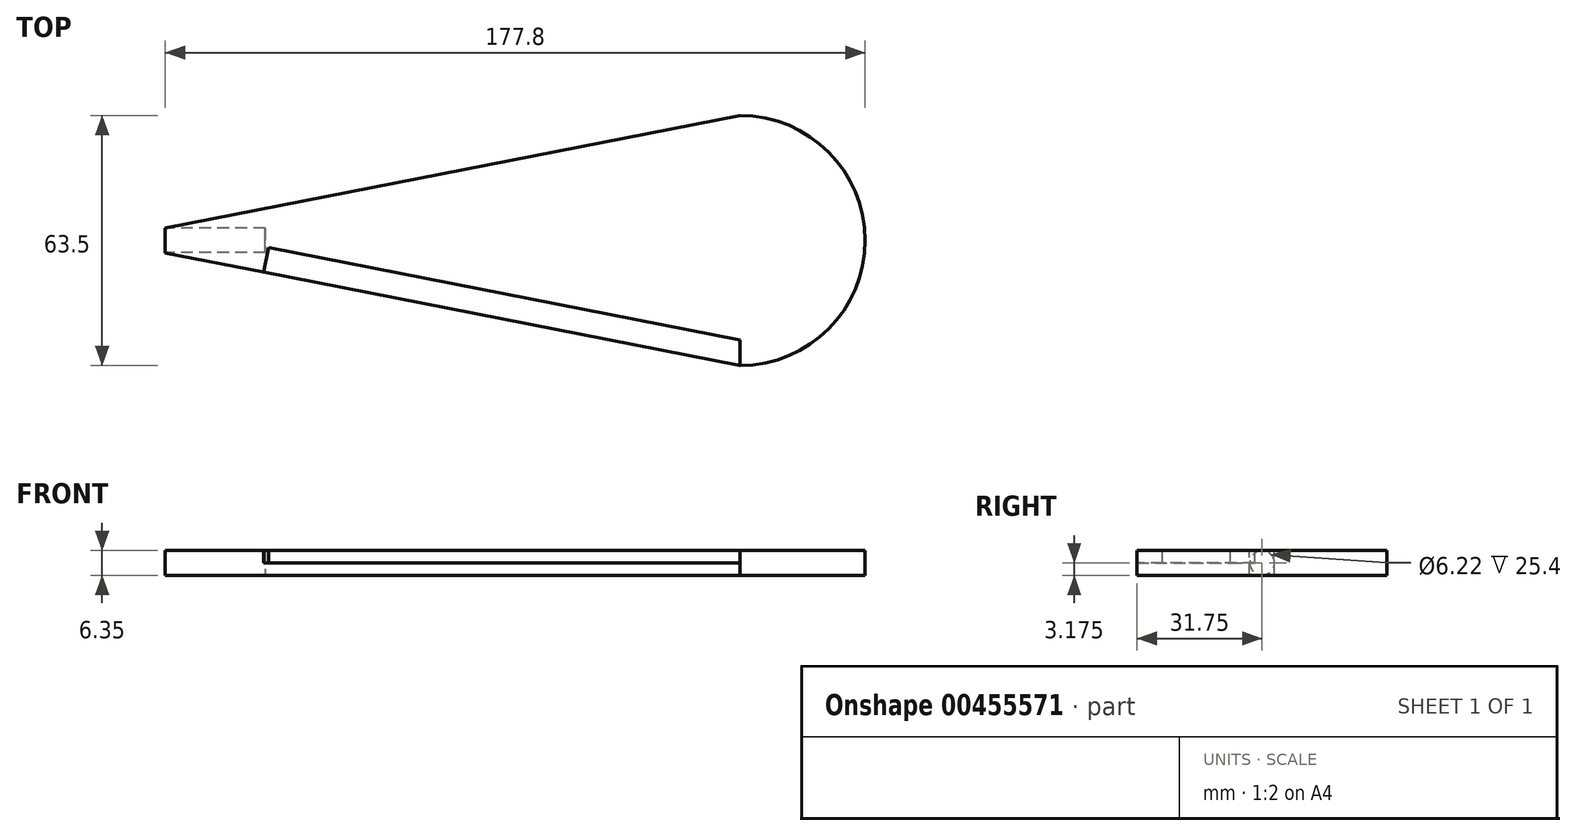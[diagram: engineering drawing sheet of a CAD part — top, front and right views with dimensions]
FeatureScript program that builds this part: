
annotation { "Feature Type Name" : "Feature", "Feature Type Description" : "" }
export const myFeature = defineFeature(function(context is Context, id is Id, definition is map)
    precondition{}
    {
        {
            var Q0;
            Q0=qCreatedBy(makeId("Top.planeOp"),FACE);
            var sketch = newSketch(context, id + "F0", { "sketchPlane" : qUnion([Q0])});
            skLineSegment(sketch, "E0", {"start": v(0, 0) * mm, "end": v(177.8, 0) * mm});
            skLineSegment(sketch, "E1", {"start": v(177.8, 0) * mm, "end": v(177.8, 63.5) * mm});
            skLineSegment(sketch, "E2", {"start": v(177.8, 63.5) * mm, "end": v(0, 63.5) * mm});
            skLineSegment(sketch, "E3", {"start": v(0, 63.5) * mm, "end": v(0, 0) * mm});
            skSolve(sketch);
        }
        {
            var Q0;
            Q0=makeQuery(id+"F0.imprint","IMPRINT",FACE,{"disambiguationData":[TD([[makeQuery(id+"F0.imprint","IMPRINT",EDGE,{"derivedFrom":sQuery(id+"F0.wireOp",EDGE,"E0")}),1.0]])]});
            extrude(context, id + "F1", {"entities" : qUnion([Q0]), "depth" : 6.35 * mm});
        }
        {
            var Q0;
            Q0=makeQuery(id+"F1.opExtrude","CAP_FACE",FACE,{"disambiguationData":[OSD([sQuery(id+"F0.wireOp",EDGE,"E0"),sQuery(id+"F0.wireOp",EDGE,"E1"),sQuery(id+"F0.wireOp",EDGE,"E2"),sQuery(id+"F0.wireOp",EDGE,"E3")])],"isStart":false});
            var sketch = newSketch(context, id + "F2", { "sketchPlane" : qUnion([Q0])});
            skArc(sketch, "E4", {"start": v(146.05, 0) * mm, "mid": v(177.8, 31.75) * mm, "end": v(146.05, 63.5) * mm});
            skSolve(sketch);
        }
        {
            var Q0;
            Q0 = qSketchRegion(id + "F2", true);
            var Q1;
            {var subQ0=sQuery(id+"F2.wireOp",EDGE,"E4");var subQ1=makeQuery(id+"F1.opExtrude","CAP_EDGE",EDGE,{"disambiguationData":[OSD([sQuery(id+"F0.wireOp",EDGE,"E2")])],"isStart":false});var subQ2=makeQuery(id+"F2.imprint","INTERSECT",VERTEX,{"derivedFrom":[subQ1,subQ0]});Q1=makeQuery(id+"F2.imprint","IMPRINT",FACE,{"disambiguationData":[TD([[makeQuery(id+"F2.imprint","IMPRINT",EDGE,{"disambiguationData":[TD([[subQ2,1.0]])],"derivedFrom":subQ0}),-1.0]])]});}
            var Q2;
            {var subQ0=sQuery(id+"F2.wireOp",EDGE,"E4");var subQ1=makeQuery(id+"F1.opExtrude","CAP_EDGE",EDGE,{"disambiguationData":[OSD([sQuery(id+"F0.wireOp",EDGE,"E0")])],"isStart":false});var subQ2=makeQuery(id+"F2.imprint","INTERSECT",VERTEX,{"derivedFrom":[subQ1,subQ0]});Q2=makeQuery(id+"F2.imprint","IMPRINT",FACE,{"disambiguationData":[TD([[makeQuery(id+"F2.imprint","IMPRINT",EDGE,{"disambiguationData":[TD([[subQ2,-1.0]])],"derivedFrom":subQ0}),-1.0]])]});}
            extrude(context, id + "F3", {"entities" : qUnion([Q0, Q1, Q2]), "operationType" : NewBodyOperationType.REMOVE, "oppositeDirection" : true, "depth" : 25.4 * mm});
        }
        {
            var Q0;
            Q0=makeQuery(id+"F1.opExtrude","CAP_FACE",FACE,{"disambiguationData":[OSD([sQuery(id+"F0.wireOp",EDGE,"E0"),sQuery(id+"F0.wireOp",EDGE,"E1"),sQuery(id+"F0.wireOp",EDGE,"E2"),sQuery(id+"F0.wireOp",EDGE,"E3")])],"isStart":false});
            var sketch = newSketch(context, id + "F4", { "sketchPlane" : qUnion([Q0])});
            skLineSegment(sketch, "E5", {"start": v(146.05, 63.5) * mm, "end": v(0, 34.93) * mm});
            skLineSegment(sketch, "E6", {"start": v(146.05, 0) * mm, "end": v(0, 28.58) * mm});
            skSolve(sketch);
        }
        {
            var Q0;
            {var subQ0=sQuery(id+"F4.wireOp",EDGE,"E5");Q0=makeQuery(id+"F4.imprint","IMPRINT",FACE,{"disambiguationData":[TD([[makeQuery(id+"F4.imprint","IMPRINT",EDGE,{"derivedFrom":subQ0}),-1.0]])]});}
            var Q1;
            {var subQ0=sQuery(id+"F4.wireOp",EDGE,"E6");Q1=makeQuery(id+"F4.imprint","IMPRINT",FACE,{"disambiguationData":[TD([[makeQuery(id+"F4.imprint","IMPRINT",EDGE,{"derivedFrom":subQ0}),1.0]])]});}
            extrude(context, id + "F5", {"entities" : qUnion([Q0, Q1]), "operationType" : NewBodyOperationType.REMOVE, "oppositeDirection" : true, "depth" : 25.4 * mm});
        }
        {
            var Q0;
            Q0=makeQuery(id+"F1.opExtrude","SWEPT_FACE",FACE,{"disambiguationData":[OSD([sQuery(id+"F0.wireOp",EDGE,"E3")])]});
            var sketch = newSketch(context, id + "F6", { "sketchPlane" : qUnion([Q0])});
            skCircle(sketch, "E7", {"center": v(-31.75, 3.17) * mm, "radius": 3.11 * mm});
            skPoint(sketch, "E7.centerSnap0", {"position": v(-31.75, 6.35) * mm});
            skPoint(sketch, "E7.centerSnap1", {"position": v(-28.58, 3.17) * mm});
            skSolve(sketch);
        }
        {
            var Q0;
            {var subQ0=sQuery(id+"F6.wireOp",EDGE,"E7");var subQ1=sQuery(id+"F0.wireOp",EDGE,"E3");var subQ2=makeQuery(id+"F6.imprint","INTERSECT",VERTEX,{"derivedFrom":[makeQuery(id+"F1.opExtrude","CAP_EDGE",EDGE,{"disambiguationData":[OSD([subQ1])],"isStart":false}),subQ0]});Q0=makeQuery(id+"F6.imprint","IMPRINT",FACE,{"disambiguationData":[TD([[makeQuery(id+"F6.imprint","IMPRINT",EDGE,{"disambiguationData":[TD([[subQ2,1.0]])],"derivedFrom":subQ0}),1.0]])]});}
            extrude(context, id + "F7", {"entities" : qUnion([Q0]), "operationType" : NewBodyOperationType.REMOVE, "oppositeDirection" : true, "depth" : 25.4 * mm});
        }
        {
            var Q0;
            Q0=makeQuery(id+"F1.opExtrude","CAP_FACE",FACE,{"disambiguationData":[OSD([sQuery(id+"F0.wireOp",EDGE,"E0"),sQuery(id+"F0.wireOp",EDGE,"E1"),sQuery(id+"F0.wireOp",EDGE,"E2"),sQuery(id+"F0.wireOp",EDGE,"E3")])],"isStart":false});
            var sketch = newSketch(context, id + "F8", { "sketchPlane" : qUnion([Q0])});
            skLineSegment(sketch, "E8", {"start": v(25.02, 23.68) * mm, "end": v(26.24, 29.91) * mm});
            skLineSegment(sketch, "E9", {"start": v(26.24, 29.91) * mm, "end": v(146.05, 6.47) * mm});
            skLineSegment(sketch, "E10", {"start": v(146.05, 6.47) * mm, "end": v(146.05, 0) * mm});
            skLineSegment(sketch, "E11", {"start": v(146.05, 0) * mm, "end": v(25.02, 23.68) * mm});
            skSolve(sketch);
        }
        {
            var Q0;
            Q0 = qSketchRegion(id + "F8", true);
            extrude(context, id + "F9", {"entities" : qUnion([Q0]), "operationType" : NewBodyOperationType.REMOVE, "oppositeDirection" : true, "depth" : 3.17 * mm});
        }
    });
